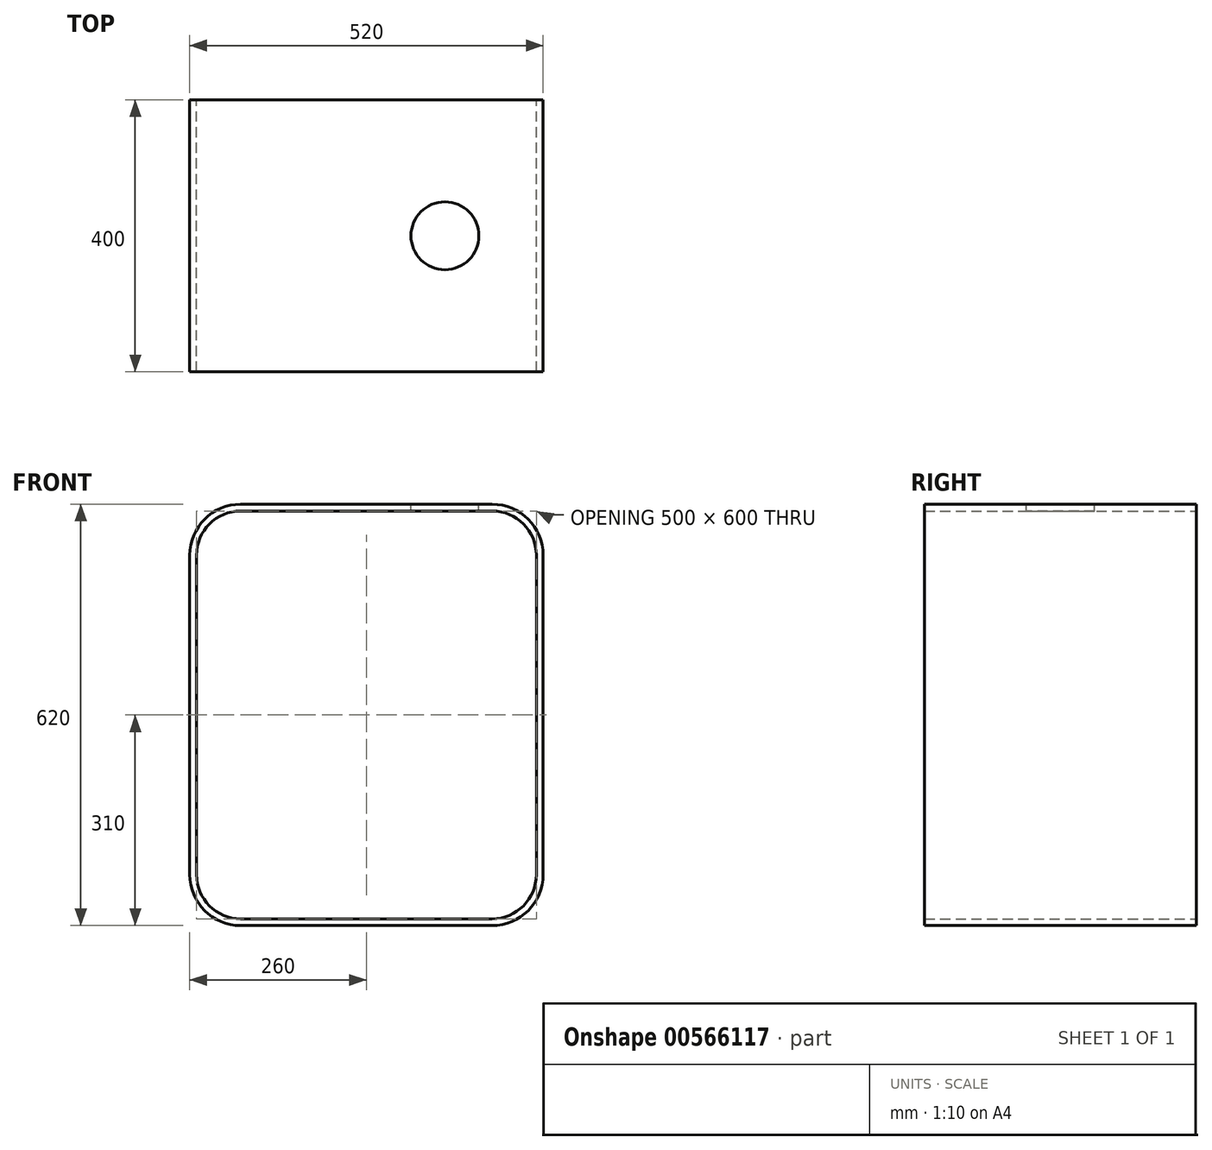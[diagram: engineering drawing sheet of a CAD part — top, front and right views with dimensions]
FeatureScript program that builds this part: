
annotation { "Feature Type Name" : "Feature", "Feature Type Description" : "" }
export const myFeature = defineFeature(function(context is Context, id is Id, definition is map)
    precondition{}
    {
        {
            var Q0;
            Q0=qCreatedBy(makeId("Front.planeOp"),FACE);
            var sketch = newSketch(context, id + "F0", { "sketchPlane" : qUnion([Q0])});
            skLineSegment(sketch, "E0.bottom", {"start": v(-185, 300) * mm, "end": v(185, 300) * mm});
            skLineSegment(sketch, "E0.top", {"start": v(-185, -300) * mm, "end": v(185, -300) * mm});
            skLineSegment(sketch, "E0.left", {"start": v(-250, 235) * mm, "end": v(-250, -235) * mm});
            skLineSegment(sketch, "E0.right", {"start": v(250, 235) * mm, "end": v(250, -235) * mm});
            skPoint(sketch, "E0.middle", {"position": v(0, 0) * mm});
            skPoint(sketch, "E1.visualSharp", {"position": v(-250, 300) * mm});
            skArc(sketch, "E1.filletArc", {"start": v(-185, 300) * mm, "mid": v(-230.96, 280.96) * mm, "end": v(-250, 235) * mm});
            skPoint(sketch, "E2.visualSharp", {"position": v(250, 300) * mm});
            skArc(sketch, "E2.filletArc", {"start": v(250, 235) * mm, "mid": v(230.96, 280.96) * mm, "end": v(185, 300) * mm});
            skPoint(sketch, "E3.visualSharp", {"position": v(-250, -300) * mm});
            skArc(sketch, "E3.filletArc", {"start": v(-250, -235) * mm, "mid": v(-230.96, -280.96) * mm, "end": v(-185, -300) * mm});
            skPoint(sketch, "E4.visualSharp", {"position": v(250, -300) * mm});
            skArc(sketch, "E4.filletArc", {"start": v(185, -300) * mm, "mid": v(230.96, -280.96) * mm, "end": v(250, -235) * mm});
            skLineSegment(sketch, "E5.0", {"start": v(260, 235) * mm, "end": v(260, -270) * mm});
            skArc(sketch, "E5.1", {"start": v(260, 235) * mm, "mid": v(238.03, 288.03) * mm, "end": v(185, 310) * mm});
            skLineSegment(sketch, "E5.2", {"start": v(-185, 310) * mm, "end": v(185, 310) * mm});
            skLineSegment(sketch, "E5.3", {"start": v(-185, -310) * mm, "end": v(220, -310) * mm});
            skArc(sketch, "E5.4", {"start": v(-260, -235) * mm, "mid": v(-238.03, -288.03) * mm, "end": v(-185, -310) * mm});
            skLineSegment(sketch, "E5.5", {"start": v(-260, 235) * mm, "end": v(-260, -235) * mm});
            skArc(sketch, "E5.6", {"start": v(-185, 310) * mm, "mid": v(-238.03, 288.03) * mm, "end": v(-260, 235) * mm});
            skArc(sketch, "E6.0", {"start": v(185, -310) * mm, "mid": v(238.03, -288.03) * mm, "end": v(260, -235) * mm});
            skSolve(sketch);
        }
        {
            var Q0;
            Q0 = qSketchRegion(id + "F0", true);
            extrude(context, id + "F1", {"entities" : qUnion([Q0]), "depth" : 400 * mm, "offsetDistance" : 25 * mm});
        }
        {
            var Q0;
            Q0=makeQuery(id+"F1.opExtrude","SWEPT_FACE",FACE,{"disambiguationData":[OSD([sQuery(id+"F0.wireOp",EDGE,"E5.2")])]});
            var sketch = newSketch(context, id + "F2", { "sketchPlane" : qUnion([Q0])});
            skLineSegment(sketch, "E7", {"start": v(0, 0) * mm, "end": v(0, -400) * mm});
            skLineSegment(sketch, "E8", {"start": v(0, -200) * mm, "end": v(-185, -200) * mm});
            skLineSegment(sketch, "E9", {"start": v(-92.5, 0) * mm, "end": v(-92.5, -200) * mm});
            skLineSegment(sketch, "E10", {"start": v(-92.5, -200) * mm, "end": v(-92.5, -400) * mm});
            skLineSegment(sketch, "E11", {"start": v(-185, -200) * mm, "end": v(-185, 0) * mm});
            skPoint(sketch, "E12.orphan", {"position": v(-185, -400) * mm});
            skPoint(sketch, "E13.right.end.orphan", {"position": v(515, -399) * mm});
            skPoint(sketch, "E13.right.start.orphan", {"position": v(550, -304) * mm});
            skCircle(sketch, "E14", {"center": v(115.52, -200) * mm, "radius": 50 * mm});
            skLineSegment(sketch, "E15", {"start": v(115.52, -324.9) * mm, "end": v(185, -400) * mm});
            skLineSegment(sketch, "E16", {"start": v(185, -324.9) * mm, "end": v(115.52, -324.9) * mm});
            skLineSegment(sketch, "E17", {"start": v(115.52, -324.9) * mm, "end": v(115.52, -250) * mm});
            skLineSegment(sketch, "E18", {"start": v(-185, -400) * mm, "end": v(-185, -200) * mm});
            skLineSegment(sketch, "E19", {"start": v(-185, -400) * mm, "end": v(185, -400) * mm});
            skLineSegment(sketch, "E20", {"start": v(-185, 0) * mm, "end": v(185, 0) * mm});
            skLineSegment(sketch, "E21", {"start": v(185, 0) * mm, "end": v(185, -400) * mm});
            skSolve(sketch);
        }
        {
            var Q0;
            Q0=makeQuery(id+"F2.imprint","IMPRINT",FACE,{"disambiguationData":[TD([[makeQuery(id+"F2.imprint","IMPRINT",EDGE,{"derivedFrom":sQuery(id+"F2.wireOp",EDGE,"E14")}),1.0]])]});
            extrude(context, id + "F3", {"entities" : qUnion([Q0]), "operationType" : NewBodyOperationType.REMOVE, "oppositeDirection" : true, "depth" : 25 * mm, "offsetDistance" : 25 * mm});
        }
    });
